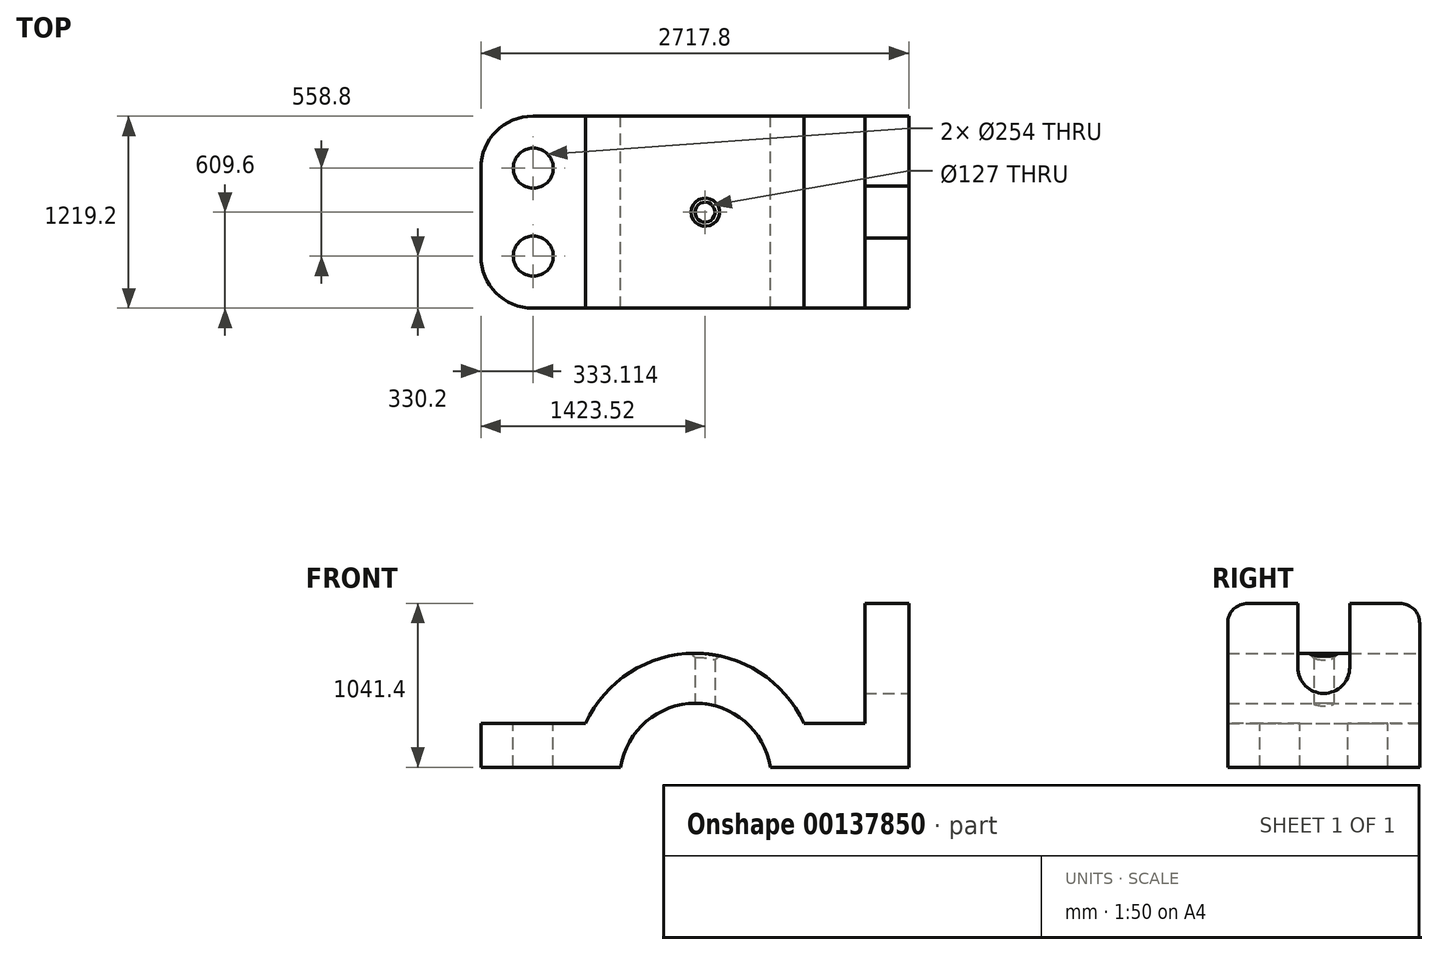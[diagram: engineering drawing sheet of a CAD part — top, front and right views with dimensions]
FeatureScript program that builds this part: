
annotation { "Feature Type Name" : "Feature", "Feature Type Description" : "" }
export const myFeature = defineFeature(function(context is Context, id is Id, definition is map)
    precondition{}
    {
        {
            var Q0;
            Q0=qCreatedBy(makeId("Front.planeOp"),FACE);
            var sketch = newSketch(context, id + "F0", { "sketchPlane" : qUnion([Q0])});
            skLineSegment(sketch, "E0", {"start": v(0, 0) * mm, "end": v(887.22, 0) * mm});
            skLineSegment(sketch, "E1", {"start": v(0, 0) * mm, "end": v(0, 279.4) * mm});
            skLineSegment(sketch, "E2", {"start": v(0, 279.4) * mm, "end": v(666.23, 279.4) * mm});
            skArc(sketch, "E3", {"start": v(2051.57, 279.4) * mm, "mid": v(1358.9, 723.83) * mm, "end": v(666.23, 279.4) * mm});
            skArc(sketch, "E4", {"start": v(1840.34, 0) * mm, "mid": v(1363.78, 406.49) * mm, "end": v(887.22, 0) * mm});
            skLineSegment(sketch, "E5", {"start": v(2051.57, 279.4) * mm, "end": v(2438.4, 279.4) * mm});
            skLineSegment(sketch, "E6", {"start": v(1840.34, 0) * mm, "end": v(2717.8, 0) * mm});
            skLineSegment(sketch, "E7", {"start": v(2717.8, 0) * mm, "end": v(2717.8, 1041.4) * mm});
            skLineSegment(sketch, "E8", {"start": v(2438.4, 279.4) * mm, "end": v(2438.4, 1041.4) * mm});
            skLineSegment(sketch, "E9", {"start": v(2438.4, 1041.4) * mm, "end": v(2717.8, 1041.4) * mm});
            skLineSegment(sketch, "E10", {"start": v(0, 0) * mm, "end": v(1358.9, 0) * mm});
            skLineSegment(sketch, "E11", {"start": v(1358.9, 0) * mm, "end": v(1358.9, 1103.93) * mm, "construction": true});
            skSolve(sketch);
        }
        {
            var Q0;
            Q0 = qSketchRegion(id + "F0", true);
            extrude(context, id + "F1", {"entities" : qUnion([Q0]), "depth" : 1219.2 * mm});
        }
        {
            var Q0;
            Q0=makeQuery(id+"F1.opExtrude","CAP_EDGE",EDGE,{"disambiguationData":[OSD([sQuery(id+"F0.wireOp",EDGE,"E9")])],"isStart":true});
            fillet(context, id + "F2", {"entities" : qUnion([Q0]), "radius" : 127 * mm, "tangentPropagation" : true, "allowEdgeOverflow" : false});
        }
        {
            var Q0;
            Q0=makeQuery(id+"F1.opExtrude","CAP_EDGE",EDGE,{"disambiguationData":[OSD([sQuery(id+"F0.wireOp",EDGE,"E9")])],"isStart":false});
            fillet(context, id + "F3", {"entities" : qUnion([Q0]), "radius" : 127 * mm, "tangentPropagation" : true, "allowEdgeOverflow" : false});
        }
        {
            var Q0;
            Q0=makeQuery(id+"F1.opExtrude","CAP_EDGE",EDGE,{"disambiguationData":[OSD([sQuery(id+"F0.wireOp",EDGE,"E1")])],"isStart":true});
            fillet(context, id + "F4", {"entities" : qUnion([Q0]), "radius" : 330.2 * mm, "tangentPropagation" : true, "allowEdgeOverflow" : false});
        }
        {
            var Q0;
            Q0=makeQuery(id+"F1.opExtrude","CAP_EDGE",EDGE,{"disambiguationData":[OSD([sQuery(id+"F0.wireOp",EDGE,"E1")])],"isStart":false});
            fillet(context, id + "F5", {"entities" : qUnion([Q0]), "radius" : 330.2 * mm, "tangentPropagation" : true, "allowEdgeOverflow" : false});
        }
        {
            var Q0;
            Q0=makeQuery(id+"F1.opExtrude","SWEPT_FACE",FACE,{"disambiguationData":[OSD([sQuery(id+"F0.wireOp",EDGE,"E7")])]});
            var sketch = newSketch(context, id + "F6", { "sketchPlane" : qUnion([Q0])});
            skLineSegment(sketch, "E12", {"start": v(-609.6, 1041.4) * mm, "end": v(-444.5, 1041.4) * mm});
            skLineSegment(sketch, "E13", {"start": v(-609.6, 1041.4) * mm, "end": v(-774.7, 1041.4) * mm});
            skLineSegment(sketch, "E14", {"start": v(-444.5, 1041.4) * mm, "end": v(-444.5, 635) * mm});
            skLineSegment(sketch, "E15", {"start": v(-774.7, 1041.4) * mm, "end": v(-774.7, 635) * mm});
            skArc(sketch, "E16", {"start": v(-774.7, 635) * mm, "mid": v(-609.6, 469.9) * mm, "end": v(-444.5, 635) * mm});
            skSolve(sketch);
        }
        {
            var Q0;
            Q0 = qSketchRegion(id + "F6", true);
            extrude(context, id + "F7", {"entities" : qUnion([Q0]), "operationType" : NewBodyOperationType.REMOVE, "oppositeDirection" : true, "depth" : 279.4 * mm});
        }
        {
            var Q0;
            Q0=makeQuery(id+"F1.opExtrude","SWEPT_FACE",FACE,{"disambiguationData":[OSD([sQuery(id+"F0.wireOp",EDGE,"E2")])]});
            var sketch = newSketch(context, id + "F8", { "sketchPlane" : qUnion([Q0])});
            skLineSegment(sketch, "E17", {"start": v(330.2, 0) * mm, "end": v(330.2, -1219.2) * mm, "construction": true});
            skLineSegment(sketch, "E18", {"start": v(0, -330.2) * mm, "end": v(666.23, -330.2) * mm, "construction": true});
            skLineSegment(sketch, "E19", {"start": v(0, -889) * mm, "end": v(666.23, -889) * mm, "construction": true});
            skCircle(sketch, "E20", {"center": v(333.11, -330.2) * mm, "radius": 127 * mm});
            skCircle(sketch, "E21", {"center": v(333.11, -889) * mm, "radius": 127 * mm});
            skSolve(sketch);
        }
        {
            var Q0;
            Q0=makeQuery(id+"F8.imprint","IMPRINT",FACE,{"disambiguationData":[TD([[makeQuery(id+"F8.imprint","IMPRINT",EDGE,{"derivedFrom":sQuery(id+"F8.wireOp",EDGE,"E20")}),1.0]])]});
            var Q1;
            Q1=makeQuery(id+"F8.imprint","IMPRINT",FACE,{"disambiguationData":[TD([[makeQuery(id+"F8.imprint","IMPRINT",EDGE,{"derivedFrom":sQuery(id+"F8.wireOp",EDGE,"E21")}),1.0]])]});
            extrude(context, id + "F9", {"entities" : qUnion([Q0, Q1]), "operationType" : NewBodyOperationType.REMOVE, "oppositeDirection" : true, "depth" : 279.4 * mm});
        }
        {
            var Q0;
            Q0=qCreatedBy(makeId("Top.planeOp"),FACE);
            var sketch = newSketch(context, id + "F10", { "sketchPlane" : qUnion([Q0])});
            skLineSegment(sketch, "E22", {"start": v(2718.92, -1218.17) * mm, "end": v(1423.52, -1218.17) * mm});
            skLineSegment(sketch, "E23", {"start": v(1423.52, -1218.17) * mm, "end": v(1423.52, -12.35) * mm});
            skLineSegment(sketch, "E24", {"start": v(683.4, -609.6) * mm, "end": v(2040.73, -609.6) * mm});
            skCircle(sketch, "E25", {"center": v(1423.52, -609.6) * mm, "radius": 63.5 * mm});
            skSolve(sketch);
        }
        {
            var Q0;
            Q0 = qSketchRegion(id + "F10", true);
            extrude(context, id + "F11", {"entities" : qUnion([Q0]), "operationType" : NewBodyOperationType.REMOVE, "depth" : 762 * mm});
        }
        {
            var Q0;
            Q0=makeQuery(id+"F11.boolean.opBoolean","INTERSECT",EDGE,{"derivedFrom":[makeQuery(id+"F1.opExtrude","SWEPT_FACE",FACE,{"disambiguationData":[OSD([sQuery(id+"F0.wireOp",EDGE,"E3")])]}),makeQuery(id+"F11.opExtrude","SWEPT_FACE",FACE,{"disambiguationData":[OSD([sQuery(id+"F10.wireOp",EDGE,"E25")])]})]});
            chamfer(context, id + "F12", {"entities" : qUnion([Q0]), "width" : 25.4 * mm, "tangentPropagation" : true});
        }
    });
